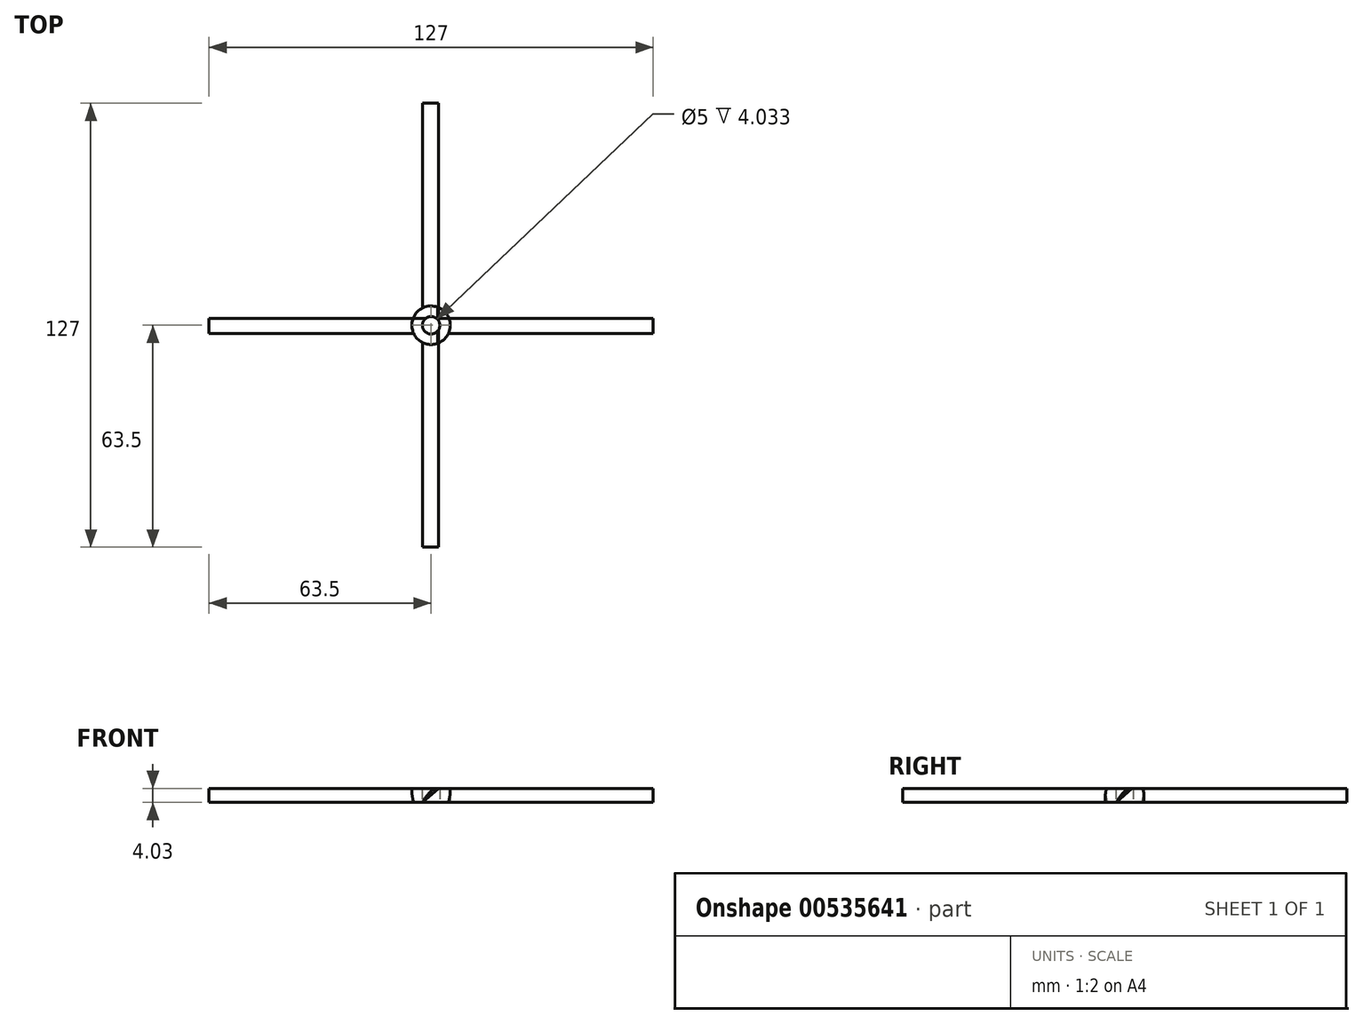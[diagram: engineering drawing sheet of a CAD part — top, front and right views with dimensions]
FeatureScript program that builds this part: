
annotation { "Feature Type Name" : "Feature", "Feature Type Description" : "" }
export const myFeature = defineFeature(function(context is Context, id is Id, definition is map)
    precondition{}
    {
        {
            var Q0;
            Q0=qCreatedBy(makeId("Top.planeOp"),FACE);
            var sketch = newSketch(context, id + "F0", { "sketchPlane" : qUnion([Q0])});
            skCircle(sketch, "E0", {"center": v(0, 0) * mm, "radius": 2.5 * mm});
            skCircle(sketch, "E1", {"center": v(0, 0) * mm, "radius": 5.5 * mm});
            skSolve(sketch);
        }
        {
            var Q0;
            Q0=makeQuery(id+"F0.imprint","IMPRINT",FACE,{"disambiguationData":[TD([[makeQuery(id+"F0.imprint","IMPRINT",EDGE,{"derivedFrom":sQuery(id+"F0.wireOp",EDGE,"E0")}),-1.0]])]});
            extrude(context, id + "F1", {"entities" : qUnion([Q0]), "depth" : 4 * mm});
        }
        {
            var Q0;
            Q0=qCreatedBy(makeId("Right.planeOp"),FACE);
            var sketch = newSketch(context, id + "F2", { "sketchPlane" : qUnion([Q0])});
            skLineSegment(sketch, "E2", {"start": v(-2.39, 0) * mm, "end": v(2, 4.03) * mm});
            skLineSegment(sketch, "E3", {"start": v(0, 0) * mm, "end": v(0, 4) * mm, "construction": true});
            skFitSpline(sketch, "E4", {"points": [v(2, 4.03) * mm, v(0, 3.13) * mm, v(-2.39, 0) * mm], "startDerivative": vector(-5.44, -2.6) * mm, "endDerivative": vector(-3.37, -5.45) * mm});
            skSolve(sketch);
        }
        {
            var Q0;
            Q0=qCreatedBy(makeId("Front.planeOp"),FACE);
            var sketch = newSketch(context, id + "F3", { "sketchPlane" : qUnion([Q0])});
            skLineSegment(sketch, "E5", {"start": v(0, 0) * mm, "end": v(0, 4) * mm, "construction": true});
            skLineSegment(sketch, "E6", {"start": v(-2.48, 0) * mm, "end": v(2.08, 4.03) * mm});
            skFitSpline(sketch, "E7", {"points": [v(2.08, 4.03) * mm, v(0.24, 3.43) * mm, v(-2.48, 0) * mm], "startDerivative": vector(-5.35, -0.91) * mm, "endDerivative": vector(-3.83, -6.88) * mm});
            skSolve(sketch);
        }
        {
            var Q0;
            Q0=makeQuery(id+"F2.imprint","IMPRINT",FACE,{"disambiguationData":[TD([[makeQuery(id+"F2.imprint","IMPRINT",EDGE,{"derivedFrom":sQuery(id+"F2.wireOp",EDGE,"E2")}),1.0]])]});
            extrude(context, id + "F4", {"entities" : qUnion([Q0]), "operationType" : NewBodyOperationType.ADD, "endBound" : BoundingType.SYMMETRIC, "depth" : 127 * mm});
        }
        {
            var Q0;
            Q0=makeQuery(id+"F3.imprint","IMPRINT",FACE,{"disambiguationData":[TD([[makeQuery(id+"F3.imprint","IMPRINT",EDGE,{"derivedFrom":sQuery(id+"F3.wireOp",EDGE,"E6")}),1.0]])]});
            extrude(context, id + "F5", {"entities" : qUnion([Q0]), "operationType" : NewBodyOperationType.ADD, "endBound" : BoundingType.SYMMETRIC, "depth" : 127 * mm});
        }
        {
            var Q0;
            Q0=makeQuery(id+"F0.imprint","IMPRINT",FACE,{"disambiguationData":[TD([[makeQuery(id+"F0.imprint","IMPRINT",EDGE,{"derivedFrom":sQuery(id+"F0.wireOp",EDGE,"E0")}),1.0]])]});
            extrude(context, id + "F6", {"entities" : qUnion([Q0]), "operationType" : NewBodyOperationType.REMOVE, "depth" : 25.4 * mm});
        }
    });
